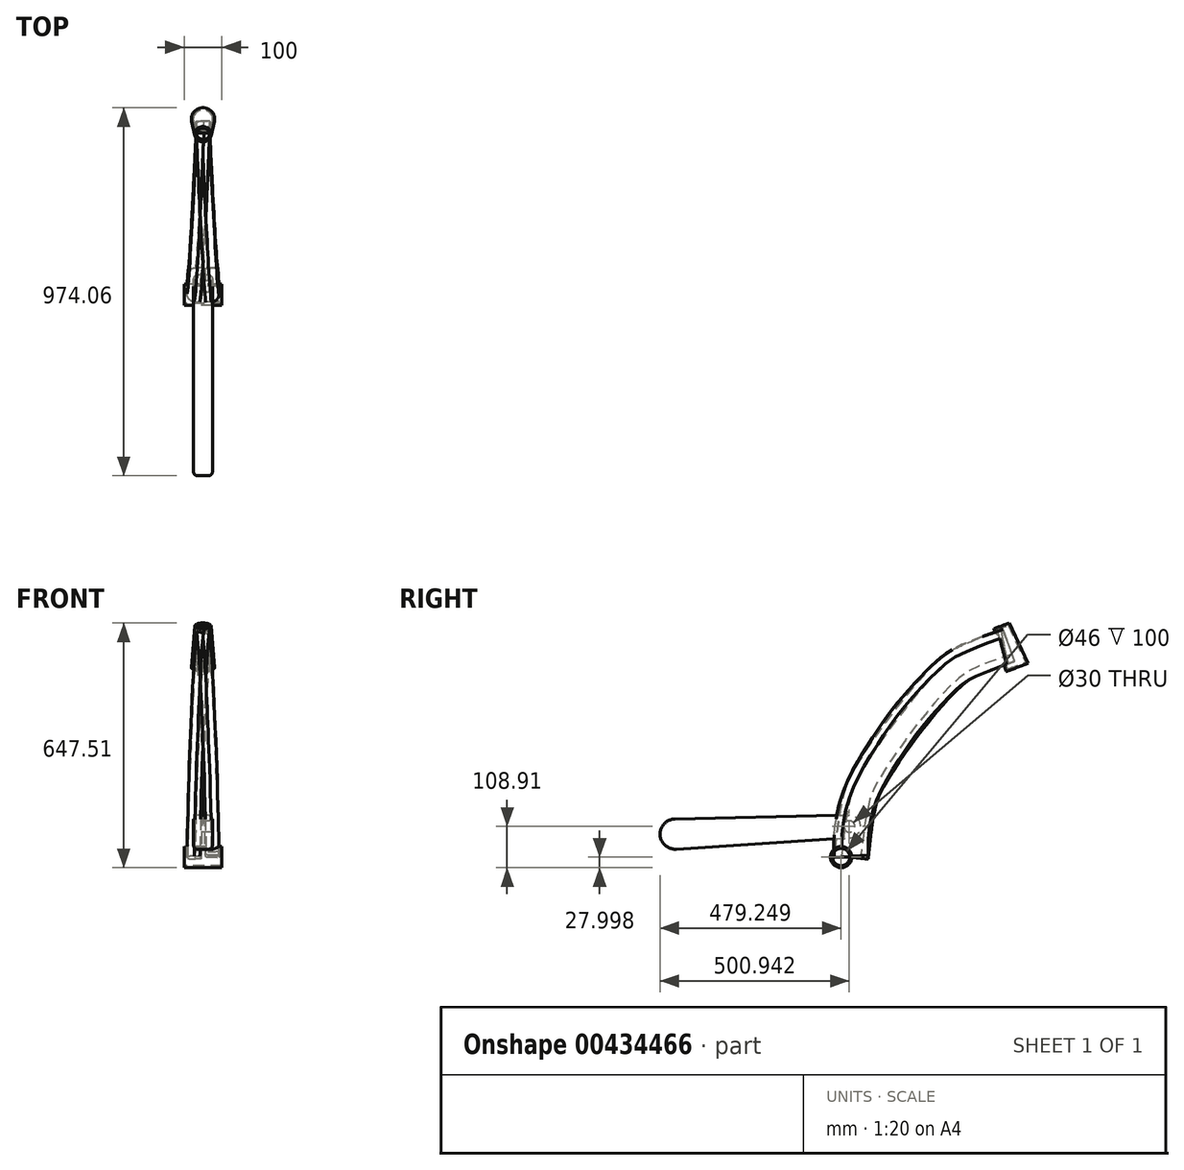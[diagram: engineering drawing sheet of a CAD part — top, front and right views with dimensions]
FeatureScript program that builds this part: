
annotation { "Feature Type Name" : "Feature", "Feature Type Description" : "" }
export const myFeature = defineFeature(function(context is Context, id is Id, definition is map)
    precondition{}
    {
        {
            assignVariable(context, id + "F0", {"name" : "BB_drop", "anyValue" : 60});
        }
        {
            var Q0;
            Q0=qCreatedBy(makeId("Right.planeOp"),FACE);
            var sketch = newSketch(context, id + "F1", { "sketchPlane" : qUnion([Q0])});
            skLineSegment(sketch, "E0", {"start": v(0, 0) * mm, "end": v(-83.68, 223.8) * mm, "construction": true});
            skLineSegment(sketch, "E1", {"start": v(-295.85, 645.65) * mm, "end": v(-16.13, -102.49) * mm, "construction": true});
            skPoint(sketch, "E2", {"position": v(-219.37, 441.1) * mm});
            skLineSegment(sketch, "E3", {"start": v(-285.85, 416.25) * mm, "end": v(-152.9, 465.96) * mm, "construction": true});
            skCircle(sketch, "E4", {"center": v(52.32, 5.34) * mm, "radius": 375.7 * mm, "construction": true});
            skPoint(sketch, "E5", {"position": v(-260.46, 551) * mm});
            skPoint(sketch, "E6", {"position": v(-683.46, -60) * mm});
            skPoint(sketch, "E7", {"position": v(-1124.4, 0) * mm});
            skLineSegment(sketch, "E8", {"start": v(-1124.4, 0) * mm, "end": v(0, 0) * mm, "construction": true});
            skCircle(sketch, "E9", {"center": v(-1124.4, 0) * mm, "radius": 375.7 * mm, "construction": true});
            skLineSegment(sketch, "E10", {"start": v(-683.46, -60) * mm, "end": v(-904.4, 662.68) * mm, "construction": true});
            skLineSegment(sketch, "E11", {"start": v(-260.46, 551) * mm, "end": v(-947.84, 551) * mm, "construction": true});
            skPoint(sketch, "E12", {"position": v(-870.26, 551) * mm});
            skLineSegment(sketch, "E13", {"start": v(-207.61, 570.76) * mm, "end": v(-313.3, 531.24) * mm, "construction": true});
            skPoint(sketch, "E14", {"position": v(-249.95, 522.9) * mm});
            skLineSegment(sketch, "E15", {"start": v(-683.46, -60) * mm, "end": v(-249.95, 522.9) * mm, "construction": true});
            skPoint(sketch, "E16", {"position": v(-785.79, 274.7) * mm});
            skLineSegment(sketch, "E17", {"start": v(-785.79, 274.7) * mm, "end": v(-249.95, 522.9) * mm, "construction": true});
            skPoint(sketch, "E18", {"position": v(-466.7, 231.45) * mm});
            skPoint(sketch, "E19", {"position": v(-517.87, 398.8) * mm});
            skSolve(sketch);
        }
        {
            var Q0;
            Q0=qCreatedBy(makeId("Right.planeOp"),FACE);
            var sketch = newSketch(context, id + "F2", { "sketchPlane" : qUnion([Q0])});
            skLineSegment(sketch, "E20", {"start": v(-243.73, 432) * mm, "end": v(-245.48, 436.69) * mm});
            skLineSegment(sketch, "E21", {"start": v(-275.1, 540.19) * mm, "end": v(-245.48, 436.69) * mm});
            skLineSegment(sketch, "E22", {"start": v(-275.1, 540.19) * mm, "end": v(-276.85, 544.87) * mm});
            skLineSegment(sketch, "E23", {"start": v(-276.85, 544.87) * mm, "end": v(-280.8, 543.4) * mm});
            skLineSegment(sketch, "E24", {"start": v(-280.8, 543.4) * mm, "end": v(-248.4, 430.25) * mm});
            skLineSegment(sketch, "E25", {"start": v(-248.4, 430.25) * mm, "end": v(-243.73, 432) * mm});
            skSolve(sketch);
        }
        {
            var Q0;
            Q0=qSketchRegion(id+"F2",true);
            var Q1;
            Q1=sQuery(id+"F1.wireOp",EDGE,"E1");
            revolve(context, id + "F3", {"entities" : qUnion([Q0]), "axis" : qUnion([Q1]), "revolveType" : RevolveType.FULL});
        }
        {
            var Q0;
            Q0=qCreatedBy(makeId("Right.planeOp"),FACE);
            var sketch = newSketch(context, id + "F4", { "sketchPlane" : qUnion([Q0])});
            skCircle(sketch, "E26", {"center": v(-685.15, -60.91) * mm, "radius": 23 * mm});
            skCircle(sketch, "E27", {"center": v(-685.15, -60.91) * mm, "radius": 28 * mm});
            skSolve(sketch);
        }
        {
            var Q0;
            Q0=qSketchRegion(id+"F4",true);
            extrude(context, id + "F5", {"entities" : qUnion([Q0]), "endBound" : BoundingType.SYMMETRIC, "depth" : 100 * mm});
        }
        {
            var Q0;
            Q0=sQuery(id+"F1.wireOp",EDGE,"E10");
            var Q1;
            Q1=sQuery(id+"F1.wireOp",VERTEX,"E16");
            cPlane(context, id + "F6", {"entities" : qUnion([Q0, Q1]), "cplaneType" : CPlaneType.LINE_POINT, "offset" : 25 * mm, "width" : 150 * mm, "height" : 150 * mm});
        }
        {
            var Q0;
            Q0=qCreatedBy(makeId("Top.planeOp"),FACE);
            cPlane(context, id + "F7", {"entities" : qUnion([Q0]), "cplaneType" : CPlaneType.OFFSET, "offset" : (getVariable(context, 'BB_drop')) * mm, "oppositeDirection" : true, "width" : 150 * mm, "height" : 150 * mm});
        }
        {
            var Q0;
            Q0=sQuery(id+"F1.wireOp",EDGE,"E1");
            cPlane(context, id + "F8", {"entities" : qUnion([Q0]), "cplaneType" : CPlaneType.LINE_ANGLE, "offset" : 25 * mm, "angle" : 90 * degree, "width" : 150 * mm, "height" : 150 * mm});
        }
        {
            var Q0;
            Q0=qCreatedBy(id+"F8.planeOp",FACE);
            var sketch = newSketch(context, id + "F9", { "sketchPlane" : qUnion([Q0])});
            skLineSegment(sketch, "E28", {"start": v(17.5, 597.32) * mm, "end": v(-17.5, 597.32) * mm});
            skLineSegment(sketch, "E29", {"start": v(-17.5, 597.32) * mm, "end": v(-17.5, 507.32) * mm});
            skLineSegment(sketch, "E30", {"start": v(-17.5, 507.32) * mm, "end": v(17.5, 507.32) * mm});
            skLineSegment(sketch, "E31", {"start": v(17.5, 507.32) * mm, "end": v(17.5, 597.32) * mm});
            skSolve(sketch);
        }
        {
            var Q0;
            Q0=qCreatedBy(id+"F7.planeOp",FACE);
            var sketch = newSketch(context, id + "F10", { "sketchPlane" : qUnion([Q0])});
            skLineSegment(sketch, "E32", {"start": v(-127.64, -683.46) * mm, "end": v(127.64, -683.46) * mm, "construction": true});
            skPoint(sketch, "E33", {"position": v(-25, -683.46) * mm});
            skPoint(sketch, "E34", {"position": v(25, -683.46) * mm});
            skSolve(sketch);
        }
        {
            var Q0;
            Q0=sQuery(id+"F1.wireOp",VERTEX,"E14");
            var Q1;
            Q1=sQuery(id+"F10.wireOp",VERTEX,"E34");
            var Q2;
            Q2=sQuery(id+"F1.wireOp",VERTEX,"E0.start");
            cPlane(context, id + "F11", {"entities" : qUnion([Q0, Q1, Q2]), "cplaneType" : CPlaneType.THREE_POINT, "offset" : 25 * mm, "width" : 150 * mm, "height" : 150 * mm});
        }
        {
            var Q0;
            Q0=sQuery(id+"F10.wireOp",VERTEX,"E33");
            var Q1;
            Q1=sQuery(id+"F1.wireOp",VERTEX,"E0.start");
            var Q2;
            Q2=sQuery(id+"F1.wireOp",VERTEX,"E14");
            cPlane(context, id + "F12", {"entities" : qUnion([Q0, Q1, Q2]), "cplaneType" : CPlaneType.THREE_POINT, "offset" : 25 * mm, "width" : 150 * mm, "height" : 150 * mm});
        }
        {
            var Q0;
            Q0=qCreatedBy(id+"F11.planeOp",FACE);
            var sketch = newSketch(context, id + "F13", { "sketchPlane" : qUnion([Q0])});
            skFitSpline(sketch, "E35", {"points": [v(250.1, 522.83) * mm, v(425.14, 436.87) * mm, v(517.13, 338.07) * mm, v(605.71, 212) * mm, v(683.88, -60.41) * mm], "startDerivative": vector(1498.65, -545) * mm, "endDerivative": vector(-79.97, -1242) * mm});
            skSolve(sketch);
        }
        {
            var Q0;
            Q0=qCreatedBy(id+"F12.planeOp",FACE);
            var sketch = newSketch(context, id + "F14", { "sketchPlane" : qUnion([Q0])});
            skFitSpline(sketch, "E36", {"points": [v(683.88, -60.41) * mm, v(628.62, 170.12) * mm, v(550.26, 285.96) * mm, v(403.75, 452.9) * mm, v(250.1, 522.83) * mm], "startDerivative": vector(-170.92, 1728.15) * mm, "endDerivative": vector(-1044.85, 369.52) * mm});
            skSolve(sketch);
        }
        {
            var Q0;
            Q0 = qSketchRegion(id + "F9", true);
            var Q1;
            Q1=sQuery(id+"F13.wireOp",EDGE,"E35");
            sweep(context, id + "F15", {"operationType" : NewBodyOperationType.ADD, "profiles" : qUnion([Q0]), "path" : qUnion([Q1])});
        }
        {
            var Q0;
            Q0 = qSketchRegion(id + "F9", true);
            var Q1;
            Q1 = qConstructionFilter(qBodyType(qCreatedBy(id + "F14" ,EDGE), BodyType.WIRE), ConstructionObject.NO);
            sweep(context, id + "F16", {"profiles" : qUnion([Q0]), "path" : qUnion([Q1])});
        }
        {
            var Q0;
            {var subQ0=sQuery(id+"F13.wireOp",EDGE,"E35");var subQ1=sQuery(id+"F9.wireOp",EDGE,"E29");var subQ2=sQuery(id+"F9.wireOp",EDGE,"E28");Q0=makeQuery(id+"F15.boolean.opBoolean","SPLIT",EDGE,{"disambiguationData":[TD([makeQuery(id+"F5.opExtrude","SWEPT_FACE",FACE,{"disambiguationData":[OSD([sQuery(id+"F4.wireOp",EDGE,"E27")])]})])],"derivedFrom":makeQuery(id+"F15.opSweep","SWEPT_EDGE",EDGE,{"disambiguationData":[OSD([subQ2,subQ1,subQ0])]})});}
            var Q1;
            Q1=makeQuery(id+"F16.opSweep","SWEPT_EDGE",EDGE,{"disambiguationData":[OSD([sQuery(id+"F9.wireOp",EDGE,"E28"),sQuery(id+"F9.wireOp",EDGE,"E31"),sQuery(id+"F14.wireOp",EDGE,"E36")])]});
            var Q2;
            {var subQ0=sQuery(id+"F13.wireOp",EDGE,"E35");var subQ1=sQuery(id+"F9.wireOp",EDGE,"E29");var subQ2=sQuery(id+"F9.wireOp",EDGE,"E30");Q2=makeQuery(id+"F15.boolean.opBoolean","SPLIT",EDGE,{"disambiguationData":[TD([makeQuery(id+"F5.opExtrude","SWEPT_FACE",FACE,{"disambiguationData":[OSD([sQuery(id+"F4.wireOp",EDGE,"E27")])]})])],"derivedFrom":makeQuery(id+"F15.opSweep","SWEPT_EDGE",EDGE,{"disambiguationData":[OSD([subQ1,subQ2,subQ0])]})});}
            var Q3;
            Q3=makeQuery(id+"F16.opSweep","SWEPT_EDGE",EDGE,{"disambiguationData":[OSD([sQuery(id+"F9.wireOp",EDGE,"E30"),sQuery(id+"F9.wireOp",EDGE,"E31"),sQuery(id+"F14.wireOp",EDGE,"E36")])]});
            fillet(context, id + "F17", {"entities" : qUnion([Q0, Q1, Q2, Q3]), "radius" : 20 * mm, "tangentPropagation" : true, "allowEdgeOverflow" : false});
        }
        {
            var Q0;
            Q0=qCreatedBy(makeId("Right.planeOp"),FACE);
            var sketch = newSketch(context, id + "F18", { "sketchPlane" : qUnion([Q0])});
            skLineSegment(sketch, "E37", {"start": v(-1125.26, 40) * mm, "end": v(-664.1, 50) * mm});
            skLineSegment(sketch, "E38", {"start": v(-1121.8, -39.92) * mm, "end": v(-661.5, -9.94) * mm});
            skArc(sketch, "E39", {"start": v(-1125.26, 40) * mm, "mid": v(-1164.36, -1.73) * mm, "end": v(-1121.8, -39.92) * mm});
            skArc(sketch, "E40", {"start": v(-661.5, -9.94) * mm, "mid": v(-633.49, 21.3) * mm, "end": v(-664.1, 50) * mm});
            skCircle(sketch, "E41", {"center": v(-663.46, 20) * mm, "radius": 15 * mm});
            skSolve(sketch);
        }
        {
            var Q0;
            Q0 = qSketchRegion(id + "F18", true);
            extrude(context, id + "F19", {"entities" : qUnion([Q0]), "endBound" : BoundingType.SYMMETRIC, "depth" : 50 * mm});
        }
        {
            var Q0;
            Q0=makeQuery(id+"F19.opExtrude","CAP_EDGE",EDGE,{"disambiguationData":[OSD([sQuery(id+"F18.wireOp",EDGE,"E37")])],"isStart":false});
            var Q1;
            Q1=makeQuery(id+"F19.opExtrude","CAP_EDGE",EDGE,{"disambiguationData":[OSD([sQuery(id+"F18.wireOp",EDGE,"E39")])],"isStart":true});
            var Q2;
            Q2=makeQuery(id+"F19.opExtrude","CAP_EDGE",EDGE,{"disambiguationData":[OSD([sQuery(id+"F18.wireOp",EDGE,"E38")])],"isStart":false});
            var Q3;
            Q3=makeQuery(id+"F19.opExtrude","CAP_EDGE",EDGE,{"disambiguationData":[OSD([sQuery(id+"F18.wireOp",EDGE,"E37")])],"isStart":true});
            var Q4;
            Q4=makeQuery(id+"F19.opExtrude","CAP_EDGE",EDGE,{"disambiguationData":[OSD([sQuery(id+"F18.wireOp",EDGE,"E40")])],"isStart":true});
            var Q5;
            Q5=makeQuery(id+"F19.opExtrude","CAP_EDGE",EDGE,{"disambiguationData":[OSD([sQuery(id+"F18.wireOp",EDGE,"E38")])],"isStart":true});
            var Q6;
            Q6=makeQuery(id+"F19.opExtrude","CAP_EDGE",EDGE,{"disambiguationData":[OSD([sQuery(id+"F18.wireOp",EDGE,"E40")])],"isStart":false});
            var Q7;
            Q7=makeQuery(id+"F19.opExtrude","CAP_EDGE",EDGE,{"disambiguationData":[OSD([sQuery(id+"F18.wireOp",EDGE,"E39")])],"isStart":false});
            fillet(context, id + "F20", {"entities" : qUnion([Q0, Q1, Q2, Q3, Q4, Q5, Q6, Q7]), "radius" : 10 * mm, "tangentPropagation" : true, "allowEdgeOverflow" : false});
        }
    });
